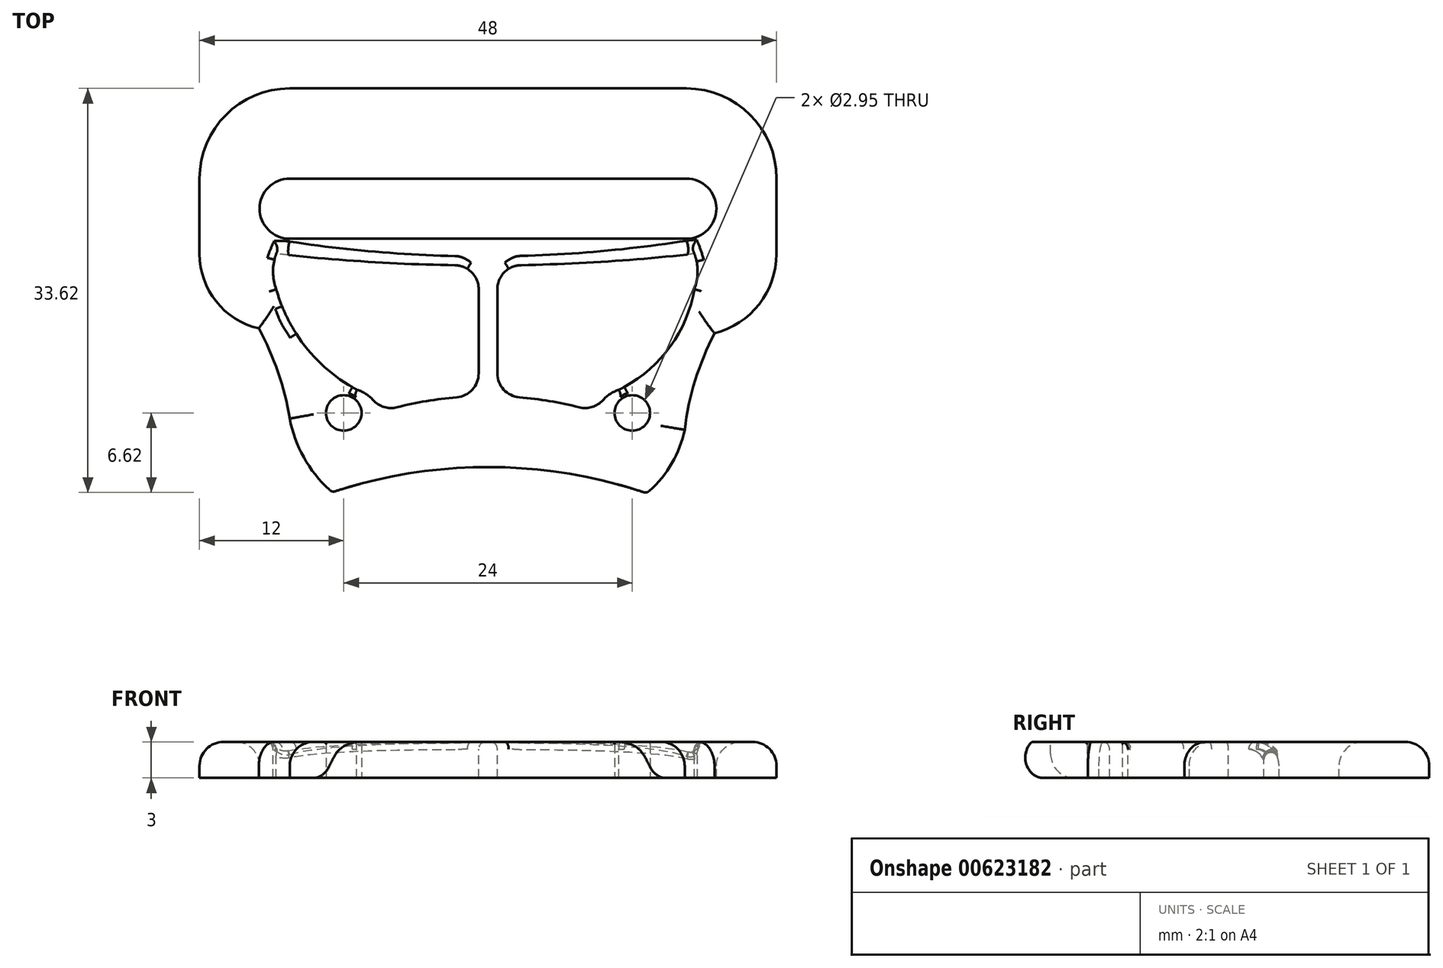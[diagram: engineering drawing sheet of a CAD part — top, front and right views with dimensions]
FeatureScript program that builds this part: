
annotation { "Feature Type Name" : "Feature", "Feature Type Description" : "" }
export const myFeature = defineFeature(function(context is Context, id is Id, definition is map)
    precondition{}
    {
        {
            var Q0;
            Q0=qCreatedBy(makeId("Top.planeOp"),FACE);
            var sketch = newSketch(context, id + "F0", { "sketchPlane" : qUnion([Q0])});
            skLineSegment(sketch, "E0.bottom", {"start": v(16.5, 2.5) * mm, "end": v(-16.5, 2.5) * mm});
            skLineSegment(sketch, "E0.top", {"start": v(16.5, -2.5) * mm, "end": v(-16.5, -2.5) * mm});
            skLineSegment(sketch, "E0.left", {"start": v(19, 0) * mm, "end": v(19, 0) * mm});
            skLineSegment(sketch, "E0.right", {"start": v(-19, 0) * mm, "end": v(-19, 0) * mm});
            skPoint(sketch, "E0.middle", {"position": v(0, 0) * mm});
            skPoint(sketch, "E1.visualSharp", {"position": v(-19, 2.5) * mm});
            skArc(sketch, "E1.filletArc", {"start": v(-16.5, 2.5) * mm, "mid": v(-18.27, 1.77) * mm, "end": v(-19, 0) * mm});
            skPoint(sketch, "E2.visualSharp", {"position": v(-19, -2.5) * mm});
            skArc(sketch, "E2.filletArc", {"start": v(-19, 0) * mm, "mid": v(-18.27, -1.77) * mm, "end": v(-16.5, -2.5) * mm});
            skPoint(sketch, "E3.visualSharp", {"position": v(19, -2.5) * mm});
            skArc(sketch, "E3.filletArc", {"start": v(16.5, -2.5) * mm, "mid": v(18.27, -1.77) * mm, "end": v(19, 0) * mm});
            skPoint(sketch, "E4.visualSharp", {"position": v(19, 2.5) * mm});
            skArc(sketch, "E4.filletArc", {"start": v(19, 0) * mm, "mid": v(18.27, 1.77) * mm, "end": v(16.5, 2.5) * mm});
            skLineSegment(sketch, "E5.bottom", {"start": v(16.5, -10) * mm, "end": v(-16.5, -10) * mm});
            skLineSegment(sketch, "E5.left", {"start": v(24, -2.5) * mm, "end": v(24, 3.75) * mm});
            skLineSegment(sketch, "E5.right", {"start": v(-24, -2.5) * mm, "end": v(-24, 3.75) * mm});
            skPoint(sketch, "E6.visualSharp", {"position": v(-24, -10) * mm});
            skArc(sketch, "E6.filletArc", {"start": v(-24, -2.5) * mm, "mid": v(-21.8, -7.8) * mm, "end": v(-16.5, -10) * mm});
            skPoint(sketch, "E7.visualSharp", {"position": v(24, -10) * mm});
            skArc(sketch, "E7.filletArc", {"start": v(16.5, -10) * mm, "mid": v(21.8, -7.8) * mm, "end": v(24, -2.5) * mm});
            skArc(sketch, "E8", {"start": v(-12.96, 23.6) * mm, "mid": v(0.12, 21.5) * mm, "end": v(13.2, 23.68) * mm});
            skLineSegment(sketch, "E9", {"start": v(0, 21.5) * mm, "end": v(0, 0) * mm, "construction": true});
            skArc(sketch, "E10", {"start": v(16.36, 18.4) * mm, "mid": v(17.24, 14.28) * mm, "end": v(18.84, 10.38) * mm});
            skArc(sketch, "E11", {"start": v(-19.07, 9.97) * mm, "mid": v(-17.47, 13.6) * mm, "end": v(-16.5, 17.47) * mm});
            skArc(sketch, "E12", {"start": v(16.5, 17.47) * mm, "mid": v(15.46, 20.9) * mm, "end": v(13.2, 23.68) * mm});
            skArc(sketch, "E13", {"start": v(-12.96, 23.6) * mm, "mid": v(-15.25, 20.83) * mm, "end": v(-16.5, 17.47) * mm});
            skArc(sketch, "E14", {"start": v(24, 3.75) * mm, "mid": v(22.56, 7.95) * mm, "end": v(18.84, 10.38) * mm});
            skArc(sketch, "E15", {"start": v(-19.07, 9.97) * mm, "mid": v(-22.62, 7.72) * mm, "end": v(-24, 3.75) * mm});
            skPoint(sketch, "E16", {"position": v(0, 10.75) * mm});
            skLineSegment(sketch, "E17.bottom", {"start": v(11.8, 3.57) * mm, "end": v(0.78, 3.57) * mm, "construction": true});
            skLineSegment(sketch, "E17.top", {"start": v(11.8, 17.93) * mm, "end": v(0.78, 17.93) * mm, "construction": true});
            skLineSegment(sketch, "E17.left", {"start": v(11.8, 3.57) * mm, "end": v(11.8, 17.93) * mm, "construction": true});
            skLineSegment(sketch, "E17.right", {"start": v(-11.8, 3.57) * mm, "end": v(-11.8, 17.93) * mm, "construction": true});
            skArc(sketch, "E18", {"start": v(-7.59, 16.53) * mm, "mid": v(-5.12, 16.01) * mm, "end": v(-2.61, 15.7) * mm});
            skArc(sketch, "E19", {"start": v(17.16, 3.75) * mm, "mid": v(9.96, 4.4) * mm, "end": v(2.74, 4.7) * mm});
            skLineSegment(sketch, "E20.bottom", {"start": v(0.78, 17.93) * mm, "end": v(-0.78, 17.93) * mm});
            skLineSegment(sketch, "E20.top", {"start": v(0.78, 3.57) * mm, "end": v(-0.78, 3.57) * mm});
            skLineSegment(sketch, "E20.left", {"start": v(0.78, 13.7) * mm, "end": v(0.78, 6.7) * mm});
            skLineSegment(sketch, "E20.right", {"start": v(-0.78, 13.7) * mm, "end": v(-0.78, 6.71) * mm});
            skArc(sketch, "E21.trimOffspring", {"start": v(2.61, 15.7) * mm, "mid": v(5.12, 16.01) * mm, "end": v(7.59, 16.53) * mm});
            skArc(sketch, "E22.trimOffspring", {"start": v(-2.75, 4.71) * mm, "mid": v(-10.2, 4.4) * mm, "end": v(-17.62, 3.75) * mm});
            skLineSegment(sketch, "E23.trimOffspring", {"start": v(-0.78, 17.93) * mm, "end": v(-11.8, 17.93) * mm, "construction": true});
            skLineSegment(sketch, "E24.trimOffspring", {"start": v(-0.78, 3.57) * mm, "end": v(-11.8, 3.57) * mm, "construction": true});
            skPoint(sketch, "E25.visualSharp", {"position": v(-0.78, 4.73) * mm});
            skArc(sketch, "E25.filletArc", {"start": v(-2.75, 4.71) * mm, "mid": v(-1.35, 5.3) * mm, "end": v(-0.78, 6.71) * mm});
            skPoint(sketch, "E26.visualSharp", {"position": v(0.78, 4.73) * mm});
            skArc(sketch, "E26.filletArc", {"start": v(0.78, 6.7) * mm, "mid": v(1.35, 5.3) * mm, "end": v(2.74, 4.7) * mm});
            skPoint(sketch, "E27.visualSharp", {"position": v(0.78, 15.6) * mm});
            skArc(sketch, "E27.filletArc", {"start": v(2.61, 15.7) * mm, "mid": v(1.3, 15.06) * mm, "end": v(0.78, 13.7) * mm});
            skPoint(sketch, "E28.visualSharp", {"position": v(-0.78, 15.6) * mm});
            skArc(sketch, "E28.filletArc", {"start": v(-0.78, 13.7) * mm, "mid": v(-1.3, 15.06) * mm, "end": v(-2.61, 15.7) * mm});
            skArc(sketch, "E29", {"start": v(-10.91, 15.06) * mm, "mid": v(-10.18, 15.4) * mm, "end": v(-9.57, 15.93) * mm});
            skArc(sketch, "E30", {"start": v(9.57, 15.93) * mm, "mid": v(10.17, 15.4) * mm, "end": v(10.9, 15.07) * mm});
            skPoint(sketch, "E31.visualSharp", {"position": v(12.01, 14.94) * mm});
            skPoint(sketch, "E32.visualSharp", {"position": v(-12.03, 14.94) * mm});
            skPoint(sketch, "E33.visualSharp", {"position": v(-8.98, 16.92) * mm});
            skArc(sketch, "E33.filletArc", {"start": v(-7.59, 16.53) * mm, "mid": v(-8.66, 16.5) * mm, "end": v(-9.57, 15.93) * mm});
            skPoint(sketch, "E34.visualSharp", {"position": v(8.98, 16.92) * mm});
            skArc(sketch, "E34.filletArc", {"start": v(9.57, 15.93) * mm, "mid": v(8.66, 16.5) * mm, "end": v(7.59, 16.53) * mm});
            skArc(sketch, "E35", {"start": v(-10.91, 15.06) * mm, "mid": v(-15.12, 11.57) * mm, "end": v(-17.62, 6.71) * mm});
            skArc(sketch, "E36", {"start": v(17.16, 6.71) * mm, "mid": v(15.04, 11.64) * mm, "end": v(10.9, 15.07) * mm});
            skArc(sketch, "E37", {"start": v(17.16, 3.75) * mm, "mid": v(17.44, 5.23) * mm, "end": v(17.16, 6.71) * mm});
            skArc(sketch, "E38", {"start": v(-17.62, 6.71) * mm, "mid": v(-17.89, 5.23) * mm, "end": v(-17.62, 3.75) * mm});
            skSolve(sketch);
        }
        {
            var Q0;
            Q0=qSketchRegion(id+"F0",true);
            extrude(context, id + "F1", {"entities" : qUnion([Q0]), "depth" : 3 * mm, "offsetDistance" : 25 * mm});
        }
        {
            var Q0;
            Q0=makeQuery(id+"F1.opExtrude","CAP_FACE",FACE,{"disambiguationData":[OSD([sQuery(id+"F0.wireOp",EDGE,"E0.bottom"),sQuery(id+"F0.wireOp",EDGE,"E0.top"),sQuery(id+"F0.wireOp",EDGE,"E1.filletArc"),sQuery(id+"F0.wireOp",EDGE,"E2.filletArc"),sQuery(id+"F0.wireOp",EDGE,"E3.filletArc"),sQuery(id+"F0.wireOp",EDGE,"E4.filletArc"),sQuery(id+"F0.wireOp",EDGE,"E5.bottom"),sQuery(id+"F0.wireOp",EDGE,"E5.left"),sQuery(id+"F0.wireOp",EDGE,"E5.right"),sQuery(id+"F0.wireOp",EDGE,"E6.filletArc"),sQuery(id+"F0.wireOp",EDGE,"E7.filletArc"),sQuery(id+"F0.wireOp",EDGE,"E8"),sQuery(id+"F0.wireOp",EDGE,"E10"),sQuery(id+"F0.wireOp",EDGE,"E11"),sQuery(id+"F0.wireOp",EDGE,"E12"),sQuery(id+"F0.wireOp",EDGE,"E13"),sQuery(id+"F0.wireOp",EDGE,"E14"),sQuery(id+"F0.wireOp",EDGE,"E15")])],"isStart":false});
            var sketch = newSketch(context, id + "F2", { "sketchPlane" : qUnion([Q0])});
            skLineSegment(sketch, "E39", {"start": v(0, 0) * mm, "end": v(0, 17) * mm, "construction": true});
            skLineSegment(sketch, "E40", {"start": v(0, 17) * mm, "end": v(-12, 17) * mm, "construction": true});
            skLineSegment(sketch, "E41", {"start": v(0, 17) * mm, "end": v(12, 17) * mm, "construction": true});
            skCircle(sketch, "E42", {"center": v(-12, 17) * mm, "radius": 1.48 * mm});
            skCircle(sketch, "E43", {"center": v(12, 17) * mm, "radius": 1.48 * mm});
            skSolve(sketch);
        }
        {
            var Q0;
            Q0=qSketchRegion(id+"F2",true);
            extrude(context, id + "F3", {"entities" : qUnion([Q0]), "operationType" : NewBodyOperationType.REMOVE, "oppositeDirection" : true, "depth" : 5 * mm, "offsetDistance" : 25 * mm});
        }
        {
            var Q0;
            Q0=makeQuery(id+"F1.opExtrude","CAP_EDGE",EDGE,{"disambiguationData":[OSD([sQuery(id+"F0.wireOp",EDGE,"E5.left")])],"isStart":true});
            var Q1;
            Q1=makeQuery(id+"F1.opExtrude","CAP_EDGE",EDGE,{"disambiguationData":[OSD([sQuery(id+"F0.wireOp",EDGE,"E7.filletArc")])],"isStart":true});
            var Q2;
            Q2=makeQuery(id+"F1.opExtrude","CAP_EDGE",EDGE,{"disambiguationData":[OSD([sQuery(id+"F0.wireOp",EDGE,"E5.bottom")])],"isStart":true});
            var Q3;
            Q3=makeQuery(id+"F1.opExtrude","CAP_EDGE",EDGE,{"disambiguationData":[OSD([sQuery(id+"F0.wireOp",EDGE,"E6.filletArc")])],"isStart":true});
            var Q4;
            Q4=makeQuery(id+"F1.opExtrude","CAP_EDGE",EDGE,{"disambiguationData":[OSD([sQuery(id+"F0.wireOp",EDGE,"E5.right")])],"isStart":true});
            var Q5;
            Q5=makeQuery(id+"F1.opExtrude","CAP_EDGE",EDGE,{"disambiguationData":[OSD([sQuery(id+"F0.wireOp",EDGE,"E15")])],"isStart":true});
            var Q6;
            Q6=makeQuery(id+"F1.opExtrude","CAP_EDGE",EDGE,{"disambiguationData":[OSD([sQuery(id+"F0.wireOp",EDGE,"E11")])],"isStart":true});
            var Q7;
            Q7=makeQuery(id+"F1.opExtrude","CAP_EDGE",EDGE,{"disambiguationData":[OSD([sQuery(id+"F0.wireOp",EDGE,"E13")])],"isStart":true});
            var Q8;
            Q8=makeQuery(id+"F1.opExtrude","CAP_EDGE",EDGE,{"disambiguationData":[OSD([sQuery(id+"F0.wireOp",EDGE,"E12")])],"isStart":true});
            var Q9;
            Q9=makeQuery(id+"F1.opExtrude","CAP_EDGE",EDGE,{"disambiguationData":[OSD([sQuery(id+"F0.wireOp",EDGE,"E10")])],"isStart":true});
            var Q10;
            Q10=makeQuery(id+"F1.opExtrude","CAP_EDGE",EDGE,{"disambiguationData":[OSD([sQuery(id+"F0.wireOp",EDGE,"E14")])],"isStart":true});
            var Q11;
            Q11=makeQuery(id+"F1.opExtrude","CAP_EDGE",EDGE,{"disambiguationData":[OSD([sQuery(id+"F0.wireOp",EDGE,"E0.bottom")])],"isStart":true});
            fillet(context, id + "F4", {"entities" : qUnion([Q0, Q1, Q2, Q3, Q4, Q5, Q6, Q7, Q8, Q9, Q10, Q11]), "radius" : 2 * mm, "tangentPropagation" : true, "allowEdgeOverflow" : false});
        }
        {
            var Q0;
            Q0=makeQuery(id+"F1.opExtrude","CAP_EDGE",EDGE,{"disambiguationData":[OSD([sQuery(id+"F0.wireOp",EDGE,"E8")])],"isStart":false});
            fillet(context, id + "F5", {"entities" : qUnion([Q0]), "radius" : 2 * mm, "tangentPropagation" : true, "allowEdgeOverflow" : false});
        }
        {
            var Q0;
            Q0=makeQuery(id+"F3.boolean.opBoolean","COPY",EDGE,{"derivedFrom":makeQuery(id+"F3.opExtrude","CAP_EDGE",EDGE,{"disambiguationData":[OSD([sQuery(id+"F2.wireOp",EDGE,"E42")])],"isStart":true})});
            var Q1;
            Q1=makeQuery(id+"F3.boolean.opBoolean","COPY",EDGE,{"derivedFrom":makeQuery(id+"F3.opExtrude","CAP_EDGE",EDGE,{"disambiguationData":[OSD([sQuery(id+"F2.wireOp",EDGE,"E43")])],"isStart":true})});
            var Q2;
            Q2=makeQuery(id+"F3.boolean.opBoolean","INTERSECT",EDGE,{"derivedFrom":[makeQuery(id+"F1.opExtrude","CAP_FACE",FACE,{"disambiguationData":[OSD([sQuery(id+"F0.wireOp",EDGE,"E0.bottom"),sQuery(id+"F0.wireOp",EDGE,"E0.top"),sQuery(id+"F0.wireOp",EDGE,"E1.filletArc"),sQuery(id+"F0.wireOp",EDGE,"E2.filletArc"),sQuery(id+"F0.wireOp",EDGE,"E3.filletArc"),sQuery(id+"F0.wireOp",EDGE,"E4.filletArc"),sQuery(id+"F0.wireOp",EDGE,"E5.bottom"),sQuery(id+"F0.wireOp",EDGE,"E5.left"),sQuery(id+"F0.wireOp",EDGE,"E5.right"),sQuery(id+"F0.wireOp",EDGE,"E6.filletArc"),sQuery(id+"F0.wireOp",EDGE,"E7.filletArc"),sQuery(id+"F0.wireOp",EDGE,"E8"),sQuery(id+"F0.wireOp",EDGE,"E10"),sQuery(id+"F0.wireOp",EDGE,"E11"),sQuery(id+"F0.wireOp",EDGE,"E12"),sQuery(id+"F0.wireOp",EDGE,"E13"),sQuery(id+"F0.wireOp",EDGE,"E14"),sQuery(id+"F0.wireOp",EDGE,"E15")])],"isStart":true}),makeQuery(id+"F3.opExtrude","SWEPT_FACE",FACE,{"disambiguationData":[OSD([sQuery(id+"F2.wireOp",EDGE,"E42")])]})]});
            var Q3;
            Q3=makeQuery(id+"F3.boolean.opBoolean","INTERSECT",EDGE,{"derivedFrom":[makeQuery(id+"F1.opExtrude","CAP_FACE",FACE,{"disambiguationData":[OSD([sQuery(id+"F0.wireOp",EDGE,"E0.bottom"),sQuery(id+"F0.wireOp",EDGE,"E0.top"),sQuery(id+"F0.wireOp",EDGE,"E1.filletArc"),sQuery(id+"F0.wireOp",EDGE,"E2.filletArc"),sQuery(id+"F0.wireOp",EDGE,"E3.filletArc"),sQuery(id+"F0.wireOp",EDGE,"E4.filletArc"),sQuery(id+"F0.wireOp",EDGE,"E5.bottom"),sQuery(id+"F0.wireOp",EDGE,"E5.left"),sQuery(id+"F0.wireOp",EDGE,"E5.right"),sQuery(id+"F0.wireOp",EDGE,"E6.filletArc"),sQuery(id+"F0.wireOp",EDGE,"E7.filletArc"),sQuery(id+"F0.wireOp",EDGE,"E8"),sQuery(id+"F0.wireOp",EDGE,"E10"),sQuery(id+"F0.wireOp",EDGE,"E11"),sQuery(id+"F0.wireOp",EDGE,"E12"),sQuery(id+"F0.wireOp",EDGE,"E13"),sQuery(id+"F0.wireOp",EDGE,"E14"),sQuery(id+"F0.wireOp",EDGE,"E15")])],"isStart":true}),makeQuery(id+"F3.opExtrude","SWEPT_FACE",FACE,{"disambiguationData":[OSD([sQuery(id+"F2.wireOp",EDGE,"E43")])]})]});
            fillet(context, id + "F6", {"entities" : qUnion([Q0, Q1, Q2, Q3]), "radius" : .2 * mm, "tangentPropagation" : true, "allowEdgeOverflow" : false});
        }
        {
            var Q0;
            Q0=makeQuery(id+"F1.opExtrude","SWEPT_BODY",BODY,{"disambiguationData":[OSD([sQuery(id+"F0.wireOp",EDGE,"E0.bottom"),sQuery(id+"F0.wireOp",EDGE,"E0.top"),sQuery(id+"F0.wireOp",EDGE,"E1.filletArc"),sQuery(id+"F0.wireOp",EDGE,"E2.filletArc"),sQuery(id+"F0.wireOp",EDGE,"E3.filletArc"),sQuery(id+"F0.wireOp",EDGE,"E4.filletArc"),sQuery(id+"F0.wireOp",EDGE,"E5.bottom"),sQuery(id+"F0.wireOp",EDGE,"E5.left"),sQuery(id+"F0.wireOp",EDGE,"E5.right"),sQuery(id+"F0.wireOp",EDGE,"E6.filletArc"),sQuery(id+"F0.wireOp",EDGE,"E7.filletArc"),sQuery(id+"F0.wireOp",EDGE,"E8"),sQuery(id+"F0.wireOp",EDGE,"E10"),sQuery(id+"F0.wireOp",EDGE,"E11"),sQuery(id+"F0.wireOp",EDGE,"E12"),sQuery(id+"F0.wireOp",EDGE,"E13"),sQuery(id+"F0.wireOp",EDGE,"E14"),sQuery(id+"F0.wireOp",EDGE,"E15")])]});
            var Q1;
            Q1=makeQuery(id+"F1.opExtrude","CAP_EDGE",EDGE,{"disambiguationData":[OSD([sQuery(id+"F0.wireOp",EDGE,"E0.bottom")])],"isStart":false});
            transform(context, id + "F7", {"entities" : qUnion([Q0]), "transformType" : TransformType.ROTATION, "transformAxis" : qUnion([Q1]), "angle" : 180 * degree, "makeCopy" : false});
        }
        {
            var Q0;
            Q0=makeQuery(id+"F1.opExtrude","CAP_EDGE",EDGE,{"disambiguationData":[OSD([sQuery(id+"F0.wireOp",EDGE,"E20.right")])],"isStart":true});
            var Q1;
            Q1=makeQuery(id+"F1.opExtrude","CAP_EDGE",EDGE,{"disambiguationData":[OSD([sQuery(id+"F0.wireOp",EDGE,"E20.left")])],"isStart":true});
            var Q2;
            Q2=makeQuery(id+"F1.opExtrude","CAP_EDGE",EDGE,{"disambiguationData":[OSD([sQuery(id+"F0.wireOp",EDGE,"E21.trimOffspring")])],"isStart":true});
            var Q3;
            Q3=makeQuery(id+"F1.opExtrude","CAP_EDGE",EDGE,{"disambiguationData":[OSD([sQuery(id+"F0.wireOp",EDGE,"E27.filletArc")])],"isStart":true});
            var Q4;
            Q4=makeQuery(id+"F1.opExtrude","CAP_EDGE",EDGE,{"disambiguationData":[OSD([sQuery(id+"F0.wireOp",EDGE,"E28.filletArc")])],"isStart":true});
            var Q5;
            Q5=makeQuery(id+"F1.opExtrude","CAP_EDGE",EDGE,{"disambiguationData":[OSD([sQuery(id+"F0.wireOp",EDGE,"E18")])],"isStart":true});
            var Q6;
            Q6=makeQuery(id+"F1.opExtrude","CAP_EDGE",EDGE,{"disambiguationData":[OSD([sQuery(id+"F0.wireOp",EDGE,"E33.filletArc")])],"isStart":true});
            var Q7;
            Q7=makeQuery(id+"F1.opExtrude","CAP_EDGE",EDGE,{"disambiguationData":[OSD([sQuery(id+"F0.wireOp",EDGE,"E29")])],"isStart":true});
            var Q8;
            Q8=makeQuery(id+"F1.opExtrude","CAP_EDGE",EDGE,{"disambiguationData":[OSD([sQuery(id+"F0.wireOp",EDGE,"E32.filletArc")])],"isStart":true});
            var Q9;
            Q9=makeQuery(id+"F1.opExtrude","CAP_EDGE",EDGE,{"disambiguationData":[OSD([sQuery(id+"F0.wireOp",EDGE,"E35")])],"isStart":true});
            var Q10;
            Q10=makeQuery(id+"F1.opExtrude","CAP_EDGE",EDGE,{"disambiguationData":[OSD([sQuery(id+"F0.wireOp",EDGE,"E38")])],"isStart":true});
            var Q11;
            Q11=makeQuery(id+"F4.opFillet","BLEND_EDGE",EDGE,{"blendedFrom":[makeQuery(id+"F1.opExtrude","CAP_EDGE",EDGE,{"disambiguationData":[OSD([sQuery(id+"F0.wireOp",EDGE,"E1.filletArc"),sQuery(id+"F0.wireOp",EDGE,"E2.filletArc")])],"isStart":true}),makeQuery(id+"F1.opExtrude","SWEPT_FACE",FACE,{"disambiguationData":[OSD([sQuery(id+"F0.wireOp",EDGE,"E38")])]})],"blendedInto":[makeQuery(id+"F1.opExtrude","SWEPT_FACE",FACE,{"disambiguationData":[OSD([sQuery(id+"F0.wireOp",EDGE,"E38")])]})]});
            var Q12;
            Q12=makeQuery(id+"F4.opFillet","BLEND_EDGE",EDGE,{"blendedFrom":[makeQuery(id+"F1.opExtrude","CAP_EDGE",EDGE,{"disambiguationData":[OSD([sQuery(id+"F0.wireOp",EDGE,"E1.filletArc"),sQuery(id+"F0.wireOp",EDGE,"E2.filletArc")])],"isStart":true}),makeQuery(id+"F1.opExtrude","SWEPT_FACE",FACE,{"disambiguationData":[OSD([sQuery(id+"F0.wireOp",EDGE,"E22.trimOffspring")])]})],"blendedInto":[makeQuery(id+"F1.opExtrude","SWEPT_FACE",FACE,{"disambiguationData":[OSD([sQuery(id+"F0.wireOp",EDGE,"E22.trimOffspring")])]})]});
            var Q13;
            Q13=makeQuery(id+"F4.opFillet","BLEND_EDGE",EDGE,{"blendedFrom":[makeQuery(id+"F1.opExtrude","CAP_EDGE",EDGE,{"disambiguationData":[OSD([sQuery(id+"F0.wireOp",EDGE,"E0.bottom")])],"isStart":true}),makeQuery(id+"F1.opExtrude","SWEPT_FACE",FACE,{"disambiguationData":[OSD([sQuery(id+"F0.wireOp",EDGE,"E22.trimOffspring")])]})],"blendedInto":[makeQuery(id+"F1.opExtrude","SWEPT_FACE",FACE,{"disambiguationData":[OSD([sQuery(id+"F0.wireOp",EDGE,"E22.trimOffspring")])]})]});
            var Q14;
            Q14=makeQuery(id+"F1.opExtrude","CAP_EDGE",EDGE,{"disambiguationData":[OSD([sQuery(id+"F0.wireOp",EDGE,"E22.trimOffspring")])],"isStart":true});
            var Q15;
            Q15=makeQuery(id+"F1.opExtrude","CAP_EDGE",EDGE,{"disambiguationData":[OSD([sQuery(id+"F0.wireOp",EDGE,"E25.filletArc")])],"isStart":true});
            var Q16;
            Q16=makeQuery(id+"F1.opExtrude","CAP_EDGE",EDGE,{"disambiguationData":[OSD([sQuery(id+"F0.wireOp",EDGE,"E26.filletArc")])],"isStart":true});
            var Q17;
            Q17=makeQuery(id+"F1.opExtrude","CAP_EDGE",EDGE,{"disambiguationData":[OSD([sQuery(id+"F0.wireOp",EDGE,"E19")])],"isStart":true});
            var Q18;
            Q18=makeQuery(id+"F4.opFillet","BLEND_EDGE",EDGE,{"blendedFrom":[makeQuery(id+"F1.opExtrude","CAP_EDGE",EDGE,{"disambiguationData":[OSD([sQuery(id+"F0.wireOp",EDGE,"E0.bottom")])],"isStart":true}),makeQuery(id+"F1.opExtrude","SWEPT_FACE",FACE,{"disambiguationData":[OSD([sQuery(id+"F0.wireOp",EDGE,"E19")])]})],"blendedInto":[makeQuery(id+"F1.opExtrude","SWEPT_FACE",FACE,{"disambiguationData":[OSD([sQuery(id+"F0.wireOp",EDGE,"E19")])]})]});
            var Q19;
            Q19=makeQuery(id+"F4.opFillet","BLEND_EDGE",EDGE,{"blendedFrom":[makeQuery(id+"F1.opExtrude","CAP_EDGE",EDGE,{"disambiguationData":[OSD([sQuery(id+"F0.wireOp",EDGE,"E3.filletArc"),sQuery(id+"F0.wireOp",EDGE,"E4.filletArc")])],"isStart":true}),makeQuery(id+"F1.opExtrude","SWEPT_FACE",FACE,{"disambiguationData":[OSD([sQuery(id+"F0.wireOp",EDGE,"E19")])]})],"blendedInto":[makeQuery(id+"F1.opExtrude","SWEPT_FACE",FACE,{"disambiguationData":[OSD([sQuery(id+"F0.wireOp",EDGE,"E19")])]})]});
            var Q20;
            Q20=makeQuery(id+"F4.opFillet","BLEND_EDGE",EDGE,{"blendedFrom":[makeQuery(id+"F1.opExtrude","CAP_EDGE",EDGE,{"disambiguationData":[OSD([sQuery(id+"F0.wireOp",EDGE,"E3.filletArc"),sQuery(id+"F0.wireOp",EDGE,"E4.filletArc")])],"isStart":true}),makeQuery(id+"F1.opExtrude","SWEPT_FACE",FACE,{"disambiguationData":[OSD([sQuery(id+"F0.wireOp",EDGE,"E37")])]})],"blendedInto":[makeQuery(id+"F1.opExtrude","SWEPT_FACE",FACE,{"disambiguationData":[OSD([sQuery(id+"F0.wireOp",EDGE,"E37")])]})]});
            var Q21;
            Q21=makeQuery(id+"F1.opExtrude","CAP_EDGE",EDGE,{"disambiguationData":[OSD([sQuery(id+"F0.wireOp",EDGE,"E37")])],"isStart":true});
            var Q22;
            Q22=makeQuery(id+"F1.opExtrude","CAP_EDGE",EDGE,{"disambiguationData":[OSD([sQuery(id+"F0.wireOp",EDGE,"E36")])],"isStart":true});
            var Q23;
            Q23=makeQuery(id+"F1.opExtrude","CAP_EDGE",EDGE,{"disambiguationData":[OSD([sQuery(id+"F0.wireOp",EDGE,"E31.filletArc")])],"isStart":true});
            var Q24;
            Q24=makeQuery(id+"F1.opExtrude","CAP_EDGE",EDGE,{"disambiguationData":[OSD([sQuery(id+"F0.wireOp",EDGE,"E30")])],"isStart":true});
            var Q25;
            Q25=makeQuery(id+"F1.opExtrude","CAP_EDGE",EDGE,{"disambiguationData":[OSD([sQuery(id+"F0.wireOp",EDGE,"E34.filletArc")])],"isStart":true});
            fillet(context, id + "F8", {"entities" : qUnion([Q0, Q1, Q2, Q3, Q4, Q5, Q6, Q7, Q8, Q9, Q10, Q11, Q12, Q13, Q14, Q15, Q16, Q17, Q18, Q19, Q20, Q21, Q22, Q23, Q24, Q25]), "radius" : .6 * mm, "allowEdgeOverflow" : false});
        }
    });
